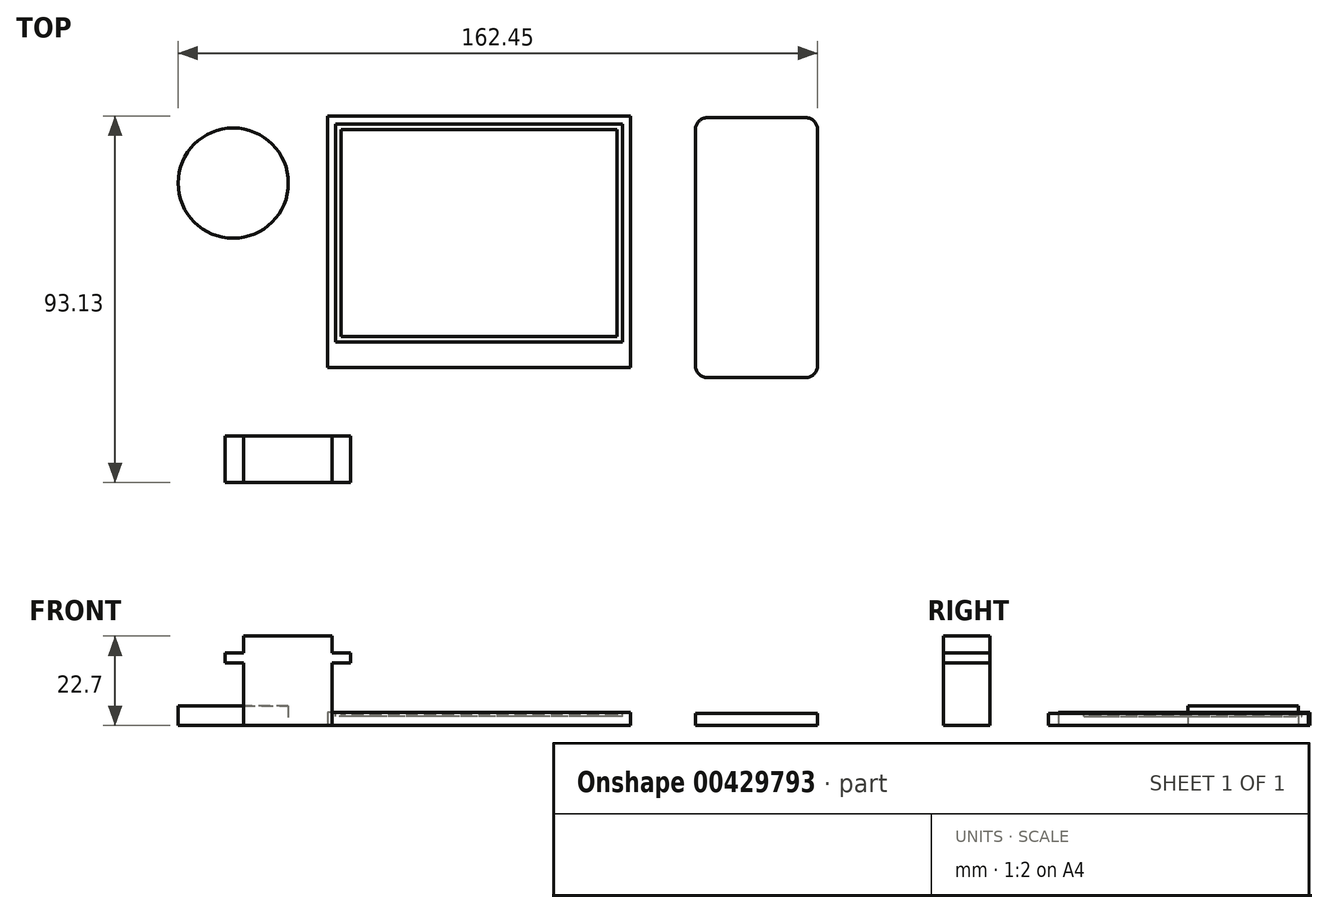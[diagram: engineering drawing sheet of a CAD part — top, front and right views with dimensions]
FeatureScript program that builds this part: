
annotation { "Feature Type Name" : "Feature", "Feature Type Description" : "" }
export const myFeature = defineFeature(function(context is Context, id is Id, definition is map)
    precondition{}
    {
        {
            var Q0;
            Q0=qCreatedBy(makeId("Top.planeOp"),FACE);
            var sketch = newSketch(context, id + "F0", { "sketchPlane" : qUnion([Q0])});
            skLineSegment(sketch, "E0.rect.bottom", {"start": v(38.45, -34.15) * mm, "end": v(-38.45, -34.15) * mm});
            skLineSegment(sketch, "E0.rect.top", {"start": v(38.45, 29.75) * mm, "end": v(-38.45, 29.75) * mm});
            skLineSegment(sketch, "E0.rect.left", {"start": v(38.45, -34.15) * mm, "end": v(38.45, 29.75) * mm});
            skLineSegment(sketch, "E0.rect.right", {"start": v(-38.45, -34.15) * mm, "end": v(-38.45, 29.75) * mm});
            skPoint(sketch, "E0.rect.middle", {"position": v(0, 0) * mm});
            skLineSegment(sketch, "E1", {"start": v(0, 29.75) * mm, "end": v(0, 0) * mm, "construction": true});
            skSolve(sketch);
        }
        {
            var Q0;
            Q0=makeQuery(id+"F0.imprint","IMPRINT",FACE,{"disambiguationData":[TD([[makeQuery(id+"F0.imprint","IMPRINT",EDGE,{"derivedFrom":sQuery(id+"F0.wireOp",EDGE,"E0.rect.bottom")}),-1.0]])]});
            extrude(context, id + "F1", {"entities" : qUnion([Q0]), "depth" : 3.3 * mm});
        }
        {
            var Q0;
            Q0=makeQuery(id+"F1.opExtrude","CAP_FACE",FACE,{"disambiguationData":[OSD([sQuery(id+"F0.wireOp",EDGE,"E0.rect.bottom"),sQuery(id+"F0.wireOp",EDGE,"E0.rect.top"),sQuery(id+"F0.wireOp",EDGE,"E0.rect.left"),sQuery(id+"F0.wireOp",EDGE,"E0.rect.right")])],"isStart":false});
            var sketch = newSketch(context, id + "F2", { "sketchPlane" : qUnion([Q0])});
            skLineSegment(sketch, "E2.rect.bottom", {"start": v(36.45, -27.7) * mm, "end": v(-36.45, -27.7) * mm});
            skLineSegment(sketch, "E2.rect.top", {"start": v(36.45, 27.7) * mm, "end": v(-36.45, 27.7) * mm});
            skLineSegment(sketch, "E2.rect.left", {"start": v(36.45, -27.7) * mm, "end": v(36.45, 27.7) * mm});
            skLineSegment(sketch, "E2.rect.right", {"start": v(-36.45, -27.7) * mm, "end": v(-36.45, 27.7) * mm});
            skPoint(sketch, "E2.rect.middle", {"position": v(0, 0) * mm});
            skSolve(sketch);
        }
        {
            var Q0;
            Q0=makeQuery(id+"F2.imprint","IMPRINT",FACE,{"disambiguationData":[TD([[makeQuery(id+"F2.imprint","IMPRINT",EDGE,{"derivedFrom":sQuery(id+"F2.wireOp",EDGE,"E2.rect.bottom")}),-1.0]])]});
            extrude(context, id + "F3", {"entities" : qUnion([Q0]), "operationType" : NewBodyOperationType.REMOVE, "oppositeDirection" : true, "depth" : 1 * mm});
        }
        {
            var Q0;
            Q0=makeQuery(id+"F3.boolean.opBoolean","COPY",FACE,{"derivedFrom":makeQuery(id+"F3.opExtrude","CAP_FACE",FACE,{"disambiguationData":[OSD([sQuery(id+"F2.wireOp",EDGE,"E2.rect.bottom"),sQuery(id+"F2.wireOp",EDGE,"E2.rect.top"),sQuery(id+"F2.wireOp",EDGE,"E2.rect.left"),sQuery(id+"F2.wireOp",EDGE,"E2.rect.right")])],"isStart":false})});
            var sketch = newSketch(context, id + "F4", { "sketchPlane" : qUnion([Q0])});
            skLineSegment(sketch, "E3.rect.bottom", {"start": v(35.04, -26.28) * mm, "end": v(-35.04, -26.28) * mm});
            skLineSegment(sketch, "E3.rect.top", {"start": v(35.04, 26.28) * mm, "end": v(-35.04, 26.28) * mm});
            skLineSegment(sketch, "E3.rect.left", {"start": v(35.04, -26.28) * mm, "end": v(35.04, 26.28) * mm});
            skLineSegment(sketch, "E3.rect.right", {"start": v(-35.04, -26.28) * mm, "end": v(-35.04, 26.28) * mm});
            skPoint(sketch, "E3.rect.middle", {"position": v(0, 0) * mm});
            skSolve(sketch);
        }
        {
            var Q0;
            Q0=makeQuery(id+"F4.imprint","IMPRINT",FACE,{"disambiguationData":[TD([[makeQuery(id+"F4.imprint","IMPRINT",EDGE,{"derivedFrom":sQuery(id+"F4.wireOp",EDGE,"E3.rect.bottom")}),-1.0]])]});
            extrude(context, id + "F5", {"entities" : qUnion([Q0]), "operationType" : NewBodyOperationType.ADD, "depth" : .5 * mm});
        }
        {
            var Q0;
            Q0=qCreatedBy(makeId("Top.planeOp"),FACE);
            var sketch = newSketch(context, id + "F6", { "sketchPlane" : qUnion([Q0])});
            skCircle(sketch, "E4", {"center": v(-62.45, 12.7) * mm, "radius": 14 * mm});
            skSolve(sketch);
        }
        {
            var Q0;
            Q0=makeQuery(id+"F6.imprint","IMPRINT",FACE,{"disambiguationData":[TD([[makeQuery(id+"F6.imprint","IMPRINT",EDGE,{"derivedFrom":sQuery(id+"F6.wireOp",EDGE,"E4")}),1.0]])]});
            extrude(context, id + "F7", {"entities" : qUnion([Q0]), "depth" : 5 * mm});
        }
        {
            var Q0;
            Q0=qCreatedBy(makeId("Top.planeOp"),FACE);
            var sketch = newSketch(context, id + "F8", { "sketchPlane" : qUnion([Q0])});
            skLineSegment(sketch, "E5.bottom", {"start": v(55, 29.32) * mm, "end": v(86, 29.32) * mm});
            skLineSegment(sketch, "E5.top", {"start": v(55, -36.68) * mm, "end": v(86, -36.68) * mm});
            skLineSegment(sketch, "E5.left", {"start": v(55, 29.32) * mm, "end": v(55, -36.68) * mm});
            skLineSegment(sketch, "E5.right", {"start": v(86, 29.32) * mm, "end": v(86, -36.68) * mm});
            skLineSegment(sketch, "E6.bottom", {"start": v(67.4, 29.32) * mm, "end": v(78.4, 29.32) * mm});
            skLineSegment(sketch, "E6.top", {"start": v(67.4, 31.32) * mm, "end": v(78.4, 31.32) * mm});
            skLineSegment(sketch, "E6.left", {"start": v(67.4, 29.32) * mm, "end": v(67.4, 31.32) * mm});
            skLineSegment(sketch, "E6.right", {"start": v(78.4, 29.32) * mm, "end": v(78.4, 31.32) * mm});
            skPoint(sketch, "E7", {"position": v(72.9, 29.32) * mm});
            skSolve(sketch);
        }
        {
            var Q0;
            Q0=makeQuery(id+"F8.imprint","IMPRINT",FACE,{"disambiguationData":[TD([[makeQuery(id+"F8.imprint","IMPRINT",EDGE,{"derivedFrom":sQuery(id+"F8.wireOp",EDGE,"E5.top")}),1.0]])]});
            var Q1;
            Q1=makeQuery(id+"F8.imprint","IMPRINT",FACE,{"disambiguationData":[TD([[makeQuery(id+"F8.imprint","IMPRINT",EDGE,{"derivedFrom":sQuery(id+"F8.wireOp",EDGE,"E6.bottom")}),1.0]])]});
            extrude(context, id + "F9", {"entities" : qUnion([Q0, Q1]), "depth" : 3 * mm});
        }
        {
            var Q0;
            Q0=makeQuery(id+"F9.opExtrude","SWEPT_EDGE",EDGE,{"disambiguationData":[OSD([sQuery(id+"F8.wireOp",EDGE,"E5.top"),sQuery(id+"F8.wireOp",EDGE,"E5.right")])]});
            var Q1;
            Q1=makeQuery(id+"F9.opExtrude","SWEPT_EDGE",EDGE,{"disambiguationData":[OSD([sQuery(id+"F8.wireOp",EDGE,"E5.top"),sQuery(id+"F8.wireOp",EDGE,"E5.left")])]});
            var Q2;
            Q2=makeQuery(id+"F9.opExtrude","SWEPT_EDGE",EDGE,{"disambiguationData":[OSD([sQuery(id+"F8.wireOp",EDGE,"E5.bottom"),sQuery(id+"F8.wireOp",EDGE,"E5.left")])]});
            var Q3;
            Q3=makeQuery(id+"F9.opExtrude","SWEPT_EDGE",EDGE,{"disambiguationData":[OSD([sQuery(id+"F8.wireOp",EDGE,"E5.bottom"),sQuery(id+"F8.wireOp",EDGE,"E5.right")])]});
            fillet(context, id + "F10", {"entities" : qUnion([Q0, Q1, Q2, Q3]), "radius" : 3 * mm, "tangentPropagation" : true, "allowEdgeOverflow" : false});
        }
        {
            var Q0;
            Q0=qCreatedBy(makeId("Top.planeOp"),FACE);
            var sketch = newSketch(context, id + "F11", { "sketchPlane" : qUnion([Q0])});
            skLineSegment(sketch, "E8.bottom", {"start": v(-37.37, -63.38) * mm, "end": v(-59.87, -63.38) * mm});
            skLineSegment(sketch, "E8.top", {"start": v(-37.37, -51.58) * mm, "end": v(-59.87, -51.58) * mm});
            skLineSegment(sketch, "E8.left", {"start": v(-37.37, -63.38) * mm, "end": v(-37.37, -51.58) * mm});
            skLineSegment(sketch, "E8.right", {"start": v(-59.87, -63.38) * mm, "end": v(-59.87, -51.58) * mm});
            skPoint(sketch, "E8.middle", {"position": v(-48.62, -57.48) * mm});
            skSolve(sketch);
        }
        {
            var Q0;
            Q0=makeQuery(id+"F11.imprint","IMPRINT",FACE,{"disambiguationData":[TD([[makeQuery(id+"F11.imprint","IMPRINT",EDGE,{"derivedFrom":sQuery(id+"F11.wireOp",EDGE,"E8.bottom")}),-1.0]])]});
            extrude(context, id + "F12", {"entities" : qUnion([Q0]), "depth" : 22.7 * mm});
        }
        {
            var Q0;
            Q0=makeQuery(id+"F12.opExtrude","SWEPT_FACE",FACE,{"disambiguationData":[OSD([sQuery(id+"F11.wireOp",EDGE,"E8.right")])]});
            var sketch = newSketch(context, id + "F13", { "sketchPlane" : qUnion([Q0])});
            skLineSegment(sketch, "E9", {"start": v(51.58, 18.4) * mm, "end": v(63.38, 18.4) * mm});
            skLineSegment(sketch, "E10", {"start": v(51.58, 15.9) * mm, "end": v(63.38, 15.9) * mm});
            skSolve(sketch);
        }
        {
            var Q0;
            {var subQ0=sQuery(id+"F13.wireOp",EDGE,"E9");Q0=makeQuery(id+"F13.imprint","IMPRINT",FACE,{"disambiguationData":[TD([[makeQuery(id+"F13.imprint","IMPRINT",EDGE,{"derivedFrom":subQ0}),-1.0]])]});}
            extrude(context, id + "F14", {"entities" : qUnion([Q0]), "operationType" : NewBodyOperationType.ADD, "depth" : 4.7 * mm});
        }
        {
            var Q0;
            Q0=makeQuery(id+"F12.opExtrude","SWEPT_FACE",FACE,{"disambiguationData":[OSD([sQuery(id+"F11.wireOp",EDGE,"E8.left")])]});
            var sketch = newSketch(context, id + "F15", { "sketchPlane" : qUnion([Q0])});
            skLineSegment(sketch, "E11", {"start": v(-63.38, 18.4) * mm, "end": v(-51.58, 18.4) * mm});
            skLineSegment(sketch, "E12", {"start": v(-63.38, 15.9) * mm, "end": v(-51.58, 15.9) * mm});
            skSolve(sketch);
        }
        {
            var Q0;
            {var subQ0=sQuery(id+"F15.wireOp",EDGE,"E11");Q0=makeQuery(id+"F15.imprint","IMPRINT",FACE,{"disambiguationData":[TD([[makeQuery(id+"F15.imprint","IMPRINT",EDGE,{"derivedFrom":subQ0}),-1.0]])]});}
            extrude(context, id + "F16", {"entities" : qUnion([Q0]), "operationType" : NewBodyOperationType.ADD, "depth" : 4.7 * mm});
        }
    });
